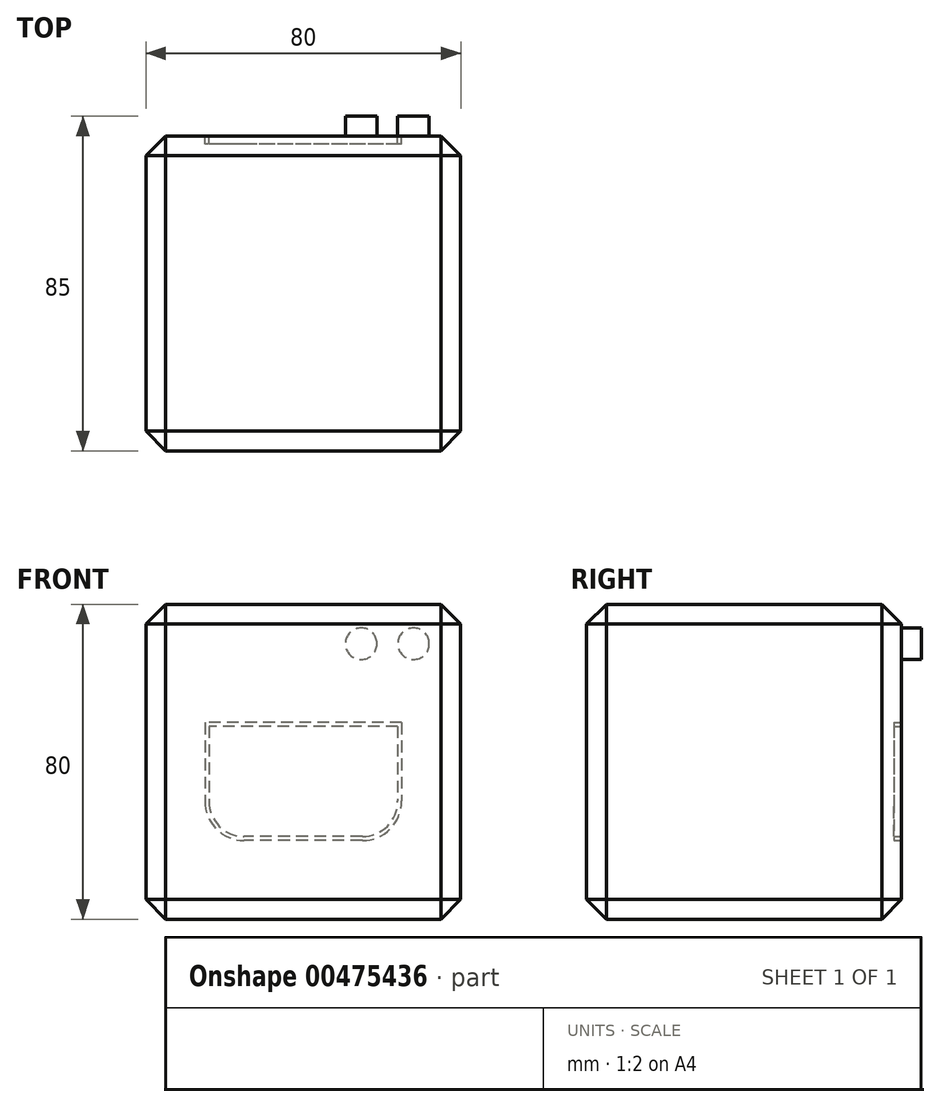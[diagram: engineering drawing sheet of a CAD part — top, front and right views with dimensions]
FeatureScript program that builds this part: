
annotation { "Feature Type Name" : "Feature", "Feature Type Description" : "" }
export const myFeature = defineFeature(function(context is Context, id is Id, definition is map)
    precondition{}
    {
        {
            var Q0;
            Q0=qCreatedBy(makeId("Top.planeOp"),FACE);
            var sketch = newSketch(context, id + "F0", { "sketchPlane" : qUnion([Q0])});
            skLineSegment(sketch, "E0.bottom", {"start": v(-54.71, 40) * mm, "end": v(25.29, 40) * mm});
            skLineSegment(sketch, "E0.top", {"start": v(-54.71, -40) * mm, "end": v(25.29, -40) * mm});
            skLineSegment(sketch, "E0.left", {"start": v(-54.71, 40) * mm, "end": v(-54.71, -40) * mm});
            skLineSegment(sketch, "E0.right", {"start": v(25.29, 40) * mm, "end": v(25.29, -40) * mm});
            skSolve(sketch);
        }
        {
            var Q0;
            Q0 = qSketchRegion(id + "F0", true);
            extrude(context, id + "F1", {"entities" : qUnion([Q0]), "depth" : 80 * mm});
        }
        {
            var Q0;
            Q0=makeQuery(id+"F1.opExtrude","SWEPT_FACE",FACE,{"disambiguationData":[OSD([sQuery(id+"F0.wireOp",EDGE,"E0.bottom")])]});
            var sketch = newSketch(context, id + "F2", { "sketchPlane" : qUnion([Q0])});
            skCircle(sketch, "E1", {"center": v(-13.29, 70) * mm, "radius": 4 * mm});
            skCircle(sketch, "E2", {"center": v(0, 70) * mm, "radius": 4 * mm});
            skSolve(sketch);
        }
        {
            var Q0;
            Q0=makeQuery(id+"F2.imprint","IMPRINT",FACE,{"disambiguationData":[TD([[makeQuery(id+"F2.imprint","IMPRINT",EDGE,{"derivedFrom":sQuery(id+"F2.wireOp",EDGE,"E2")}),1.0]])]});
            var Q1;
            Q1=makeQuery(id+"F2.imprint","IMPRINT",FACE,{"disambiguationData":[TD([[makeQuery(id+"F2.imprint","IMPRINT",EDGE,{"derivedFrom":sQuery(id+"F2.wireOp",EDGE,"E1")}),1.0]])]});
            extrude(context, id + "F3", {"entities" : qUnion([Q0, Q1]), "operationType" : NewBodyOperationType.ADD, "depth" : 5 * mm});
        }
        {
            var Q0;
            Q0=makeQuery(id+"F1.opExtrude","SWEPT_FACE",FACE,{"disambiguationData":[OSD([sQuery(id+"F0.wireOp",EDGE,"E0.bottom")])]});
            var sketch = newSketch(context, id + "F4", { "sketchPlane" : qUnion([Q0])});
            skLineSegment(sketch, "E3.bottom", {"start": v(-10.29, 50) * mm, "end": v(39.71, 50) * mm});
            skLineSegment(sketch, "E3.top", {"start": v(-0.29, 20) * mm, "end": v(29.71, 20) * mm});
            skLineSegment(sketch, "E3.left", {"start": v(-10.29, 50) * mm, "end": v(-10.29, 30) * mm});
            skLineSegment(sketch, "E3.right", {"start": v(39.71, 50) * mm, "end": v(39.71, 30) * mm});
            skPoint(sketch, "E4.visualSharp", {"position": v(-10.29, 20) * mm});
            skArc(sketch, "E4.filletArc", {"start": v(-10.29, 30) * mm, "mid": v(-7.36, 22.93) * mm, "end": v(-0.29, 20) * mm});
            skPoint(sketch, "E5.visualSharp", {"position": v(39.71, 20) * mm});
            skArc(sketch, "E5.filletArc", {"start": v(29.71, 20) * mm, "mid": v(36.79, 22.93) * mm, "end": v(39.71, 30) * mm});
            skPoint(sketch, "E6.visualSharp", {"position": v(-8.29, 14.64) * mm});
            skLineSegment(sketch, "E7.bottom", {"start": v(-9.29, 49) * mm, "end": v(38.71, 49) * mm});
            skLineSegment(sketch, "E7.top", {"start": v(-0.29, 21) * mm, "end": v(29.71, 21) * mm});
            skLineSegment(sketch, "E7.left", {"start": v(-9.29, 49) * mm, "end": v(-9.29, 30) * mm});
            skLineSegment(sketch, "E7.right", {"start": v(38.71, 49) * mm, "end": v(38.71, 30) * mm});
            skPoint(sketch, "E8.visualSharp", {"position": v(-9.29, 21) * mm});
            skArc(sketch, "E8.filletArc", {"start": v(-9.29, 30) * mm, "mid": v(-6.65, 23.64) * mm, "end": v(-0.29, 21) * mm});
            skPoint(sketch, "E9.visualSharp", {"position": v(38.71, 21) * mm});
            skArc(sketch, "E9.filletArc", {"start": v(29.71, 21) * mm, "mid": v(36.08, 23.64) * mm, "end": v(38.71, 30) * mm});
            skSolve(sketch);
        }
        {
            var Q0;
            Q0 = qSketchRegion(id + "F4", true);
            extrude(context, id + "F5", {"entities" : qUnion([Q0]), "operationType" : NewBodyOperationType.REMOVE, "oppositeDirection" : true, "depth" : 2 * mm});
        }
        {
            var Q0;
            Q0=makeQuery(id+"F1.opExtrude","CAP_EDGE",EDGE,{"disambiguationData":[OSD([sQuery(id+"F0.wireOp",EDGE,"E0.top")])],"isStart":true});
            var Q1;
            Q1=makeQuery(id+"F1.opExtrude","CAP_EDGE",EDGE,{"disambiguationData":[OSD([sQuery(id+"F0.wireOp",EDGE,"E0.right")])],"isStart":true});
            var Q2;
            Q2=makeQuery(id+"F1.opExtrude","SWEPT_FACE",FACE,{"disambiguationData":[OSD([sQuery(id+"F0.wireOp",EDGE,"E0.right")])]});
            var Q3;
            Q3=makeQuery(id+"F1.opExtrude","SWEPT_EDGE",EDGE,{"disambiguationData":[OSD([sQuery(id+"F0.wireOp",EDGE,"E0.bottom"),sQuery(id+"F0.wireOp",EDGE,"E0.left")])]});
            var Q4;
            Q4=makeQuery(id+"F1.opExtrude","CAP_FACE",FACE,{"disambiguationData":[OSD([sQuery(id+"F0.wireOp",EDGE,"E0.bottom"),sQuery(id+"F0.wireOp",EDGE,"E0.top"),sQuery(id+"F0.wireOp",EDGE,"E0.left"),sQuery(id+"F0.wireOp",EDGE,"E0.right")])],"isStart":true});
            var Q5;
            Q5=makeQuery(id+"F1.opExtrude","CAP_EDGE",EDGE,{"disambiguationData":[OSD([sQuery(id+"F0.wireOp",EDGE,"E0.left")])],"isStart":false});
            var Q6;
            Q6=makeQuery(id+"F1.opExtrude","CAP_EDGE",EDGE,{"disambiguationData":[OSD([sQuery(id+"F0.wireOp",EDGE,"E0.bottom")])],"isStart":false});
            var Q7;
            Q7=makeQuery(id+"F1.opExtrude","CAP_EDGE",EDGE,{"disambiguationData":[OSD([sQuery(id+"F0.wireOp",EDGE,"E0.top")])],"isStart":false});
            var Q8;
            Q8=makeQuery(id+"F1.opExtrude","SWEPT_EDGE",EDGE,{"disambiguationData":[OSD([sQuery(id+"F0.wireOp",EDGE,"E0.top"),sQuery(id+"F0.wireOp",EDGE,"E0.left")])]});
            chamfer(context, id + "F6", {"entities" : qUnion([Q0, Q1, Q2, Q3, Q4, Q5, Q6, Q7, Q8]), "width" : 5 * mm, "tangentPropagation" : true});
        }
    });
